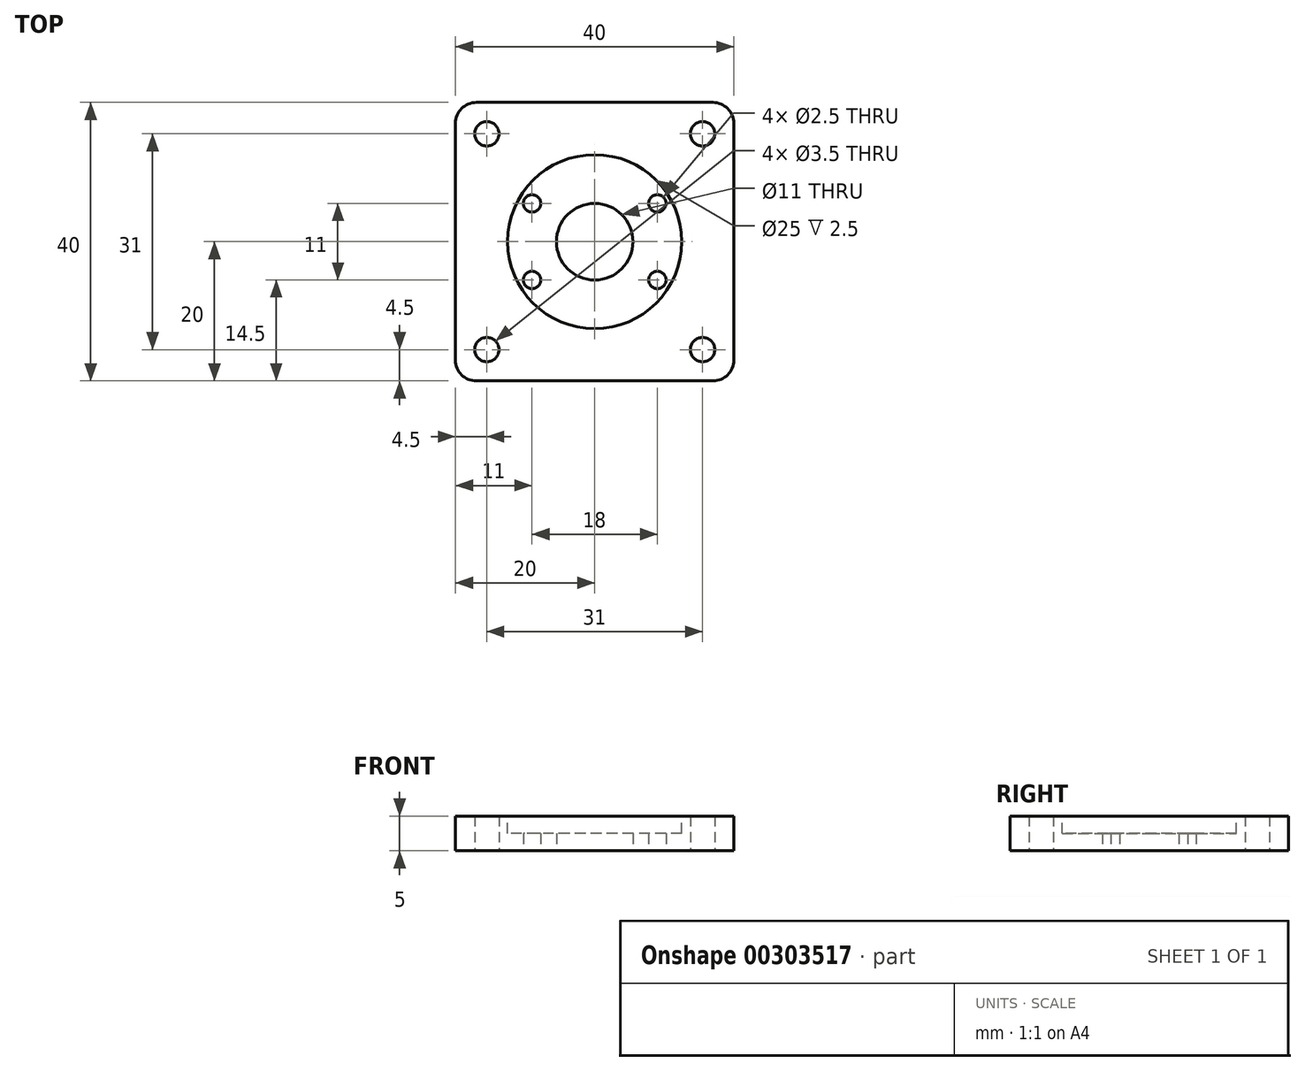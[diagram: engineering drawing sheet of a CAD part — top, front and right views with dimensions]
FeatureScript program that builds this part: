
annotation { "Feature Type Name" : "Feature", "Feature Type Description" : "" }
export const myFeature = defineFeature(function(context is Context, id is Id, definition is map)
    precondition{}
    {
        {
            var Q0;
            Q0=qCreatedBy(makeId("Top.planeOp"),FACE);
            var sketch = newSketch(context, id + "F0", { "sketchPlane" : qUnion([Q0])});
            skLineSegment(sketch, "E0.bottom", {"start": v(-20, 20) * mm, "end": v(20, 20) * mm});
            skLineSegment(sketch, "E0.top", {"start": v(-20, -20) * mm, "end": v(20, -20) * mm});
            skLineSegment(sketch, "E0.left", {"start": v(-20, 20) * mm, "end": v(-20, -20) * mm});
            skLineSegment(sketch, "E0.right", {"start": v(20, 20) * mm, "end": v(20, -20) * mm});
            skCircle(sketch, "E1", {"center": v(-15.5, 15.5) * mm, "radius": 1.75 * mm});
            skCircle(sketch, "E2", {"center": v(15.5, 15.5) * mm, "radius": 1.75 * mm});
            skCircle(sketch, "E3", {"center": v(15.5, -15.5) * mm, "radius": 1.75 * mm});
            skCircle(sketch, "E4", {"center": v(-15.5, -15.5) * mm, "radius": 1.75 * mm});
            skCircle(sketch, "E5", {"center": v(-9, -5.5) * mm, "radius": 1.25 * mm});
            skCircle(sketch, "E6", {"center": v(9, -5.5) * mm, "radius": 1.25 * mm});
            skCircle(sketch, "E7", {"center": v(9, 5.5) * mm, "radius": 1.25 * mm});
            skCircle(sketch, "E8", {"center": v(-9, 5.5) * mm, "radius": 1.25 * mm});
            skCircle(sketch, "E9", {"center": v(0, 0) * mm, "radius": 5.5 * mm});
            skSolve(sketch);
        }
        {
            var Q0;
            Q0=makeQuery(id+"F0.imprint","IMPRINT",FACE,{"disambiguationData":[TD([[makeQuery(id+"F0.imprint","IMPRINT",EDGE,{"derivedFrom":sQuery(id+"F0.wireOp",EDGE,"E0.bottom")}),-1.0]])]});
            extrude(context, id + "F1", {"entities" : qUnion([Q0]), "depth" : 5 * mm});
        }
        {
            var Q0;
            Q0=makeQuery(id+"F1.opExtrude","CAP_FACE",FACE,{"disambiguationData":[OSD([sQuery(id+"F0.wireOp",EDGE,"E0.bottom"),sQuery(id+"F0.wireOp",EDGE,"E0.top"),sQuery(id+"F0.wireOp",EDGE,"E0.left"),sQuery(id+"F0.wireOp",EDGE,"E0.right"),sQuery(id+"F0.wireOp",EDGE,"E1"),sQuery(id+"F0.wireOp",EDGE,"E2"),sQuery(id+"F0.wireOp",EDGE,"E3"),sQuery(id+"F0.wireOp",EDGE,"E4"),sQuery(id+"F0.wireOp",EDGE,"E5"),sQuery(id+"F0.wireOp",EDGE,"E6"),sQuery(id+"F0.wireOp",EDGE,"E7"),sQuery(id+"F0.wireOp",EDGE,"E8")])],"isStart":false});
            var sketch = newSketch(context, id + "F2", { "sketchPlane" : qUnion([Q0])});
            skCircle(sketch, "E10", {"center": v(0, 0) * mm, "radius": 12.5 * mm});
            skSolve(sketch);
        }
        {
            var Q0;
            Q0 = qSketchRegion(id + "F2", true);
            extrude(context, id + "F3", {"entities" : qUnion([Q0]), "operationType" : NewBodyOperationType.REMOVE, "oppositeDirection" : true, "depth" : 2.5 * mm});
        }
        {
            var Q0;
            Q0=makeQuery(id+"F1.opExtrude","SWEPT_EDGE",EDGE,{"disambiguationData":[OSD([sQuery(id+"F0.wireOp",EDGE,"E0.top"),sQuery(id+"F0.wireOp",EDGE,"E0.left")])]});
            var Q1;
            Q1=makeQuery(id+"F1.opExtrude","SWEPT_EDGE",EDGE,{"disambiguationData":[OSD([sQuery(id+"F0.wireOp",EDGE,"E0.top"),sQuery(id+"F0.wireOp",EDGE,"E0.right")])]});
            var Q2;
            Q2=makeQuery(id+"F1.opExtrude","SWEPT_EDGE",EDGE,{"disambiguationData":[OSD([sQuery(id+"F0.wireOp",EDGE,"E0.bottom"),sQuery(id+"F0.wireOp",EDGE,"E0.right")])]});
            var Q3;
            Q3=makeQuery(id+"F1.opExtrude","SWEPT_EDGE",EDGE,{"disambiguationData":[OSD([sQuery(id+"F0.wireOp",EDGE,"E0.bottom"),sQuery(id+"F0.wireOp",EDGE,"E0.left")])]});
            fillet(context, id + "F4", {"entities" : qUnion([Q0, Q1, Q2, Q3]), "radius" : 3 * mm, "tangentPropagation" : true, "allowEdgeOverflow" : false});
        }
    });
